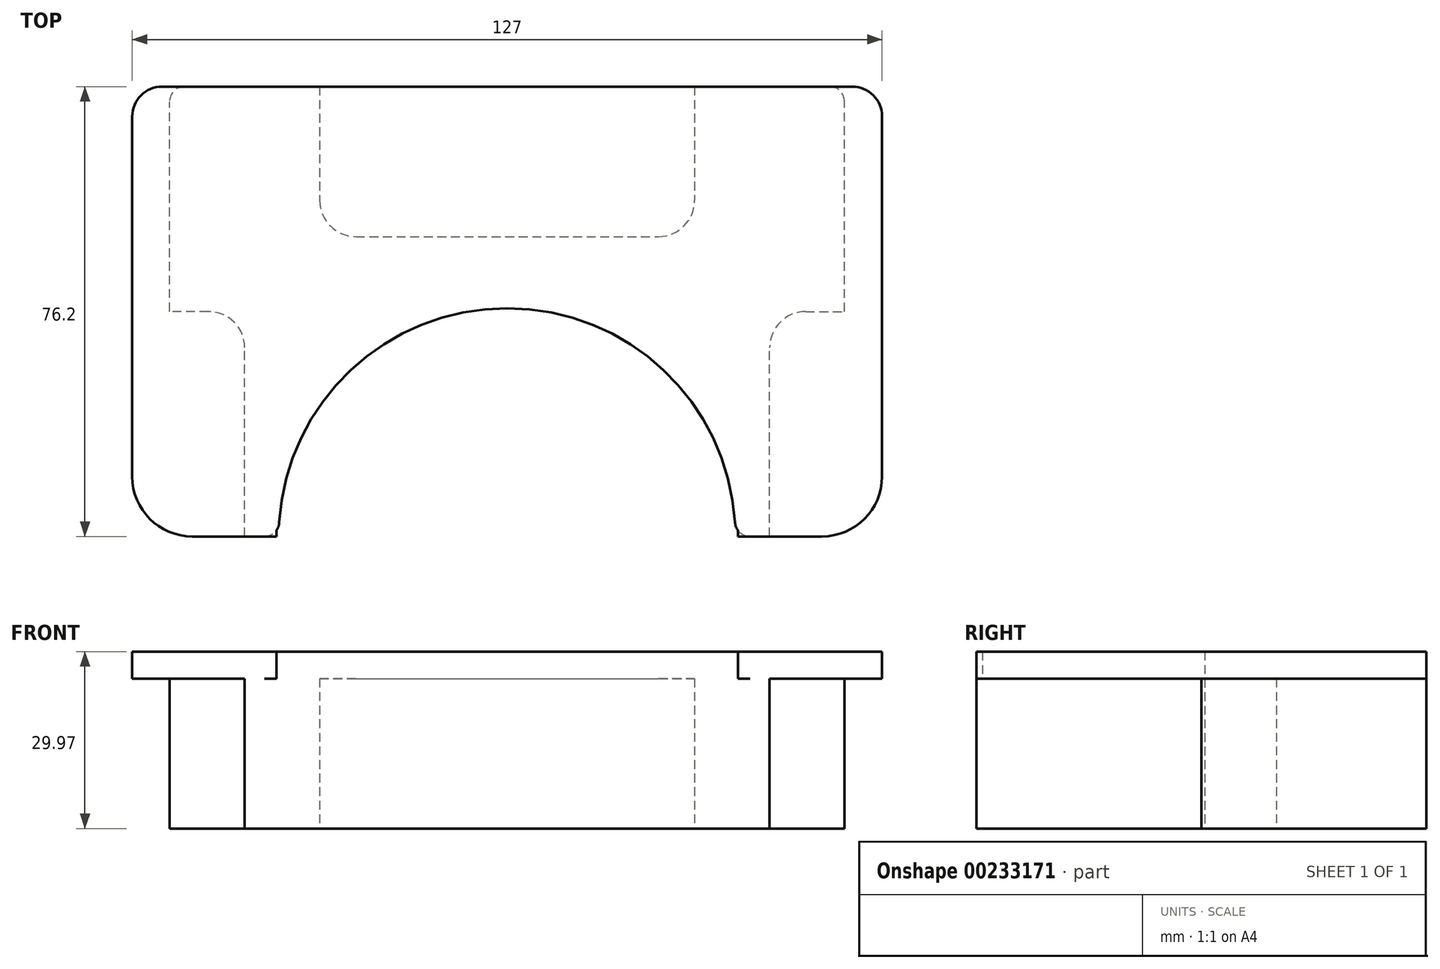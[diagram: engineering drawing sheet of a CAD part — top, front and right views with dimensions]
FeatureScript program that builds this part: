
annotation { "Feature Type Name" : "Feature", "Feature Type Description" : "" }
export const myFeature = defineFeature(function(context is Context, id is Id, definition is map)
    precondition{}
    {
        {
            var Q0;
            Q0=qCreatedBy(makeId("Top.planeOp"),FACE);
            var sketch = newSketch(context, id + "F0", { "sketchPlane" : qUnion([Q0])});
            skLineSegment(sketch, "E0.bottom", {"start": v(-63.5, 38.1) * mm, "end": v(63.5, 38.1) * mm});
            skLineSegment(sketch, "E0.top", {"start": v(-63.5, -38.1) * mm, "end": v(63.5, -38.1) * mm});
            skLineSegment(sketch, "E0.left", {"start": v(-63.5, 38.1) * mm, "end": v(-63.5, -38.1) * mm});
            skLineSegment(sketch, "E0.right", {"start": v(63.5, 38.1) * mm, "end": v(63.5, -38.1) * mm});
            skPoint(sketch, "E0.middle", {"position": v(0, 0) * mm});
            skSolve(sketch);
        }
        {
            var Q0;
            Q0 = qSketchRegion(id + "F0", true);
            extrude(context, id + "F1", {"entities" : qUnion([Q0]), "depth" : 4.57 * mm});
        }
        {
            var Q0;
            Q0=makeQuery(id+"F1.opExtrude","CAP_FACE",FACE,{"disambiguationData":[OSD([sQuery(id+"F0.wireOp",EDGE,"E0.bottom"),sQuery(id+"F0.wireOp",EDGE,"E0.top"),sQuery(id+"F0.wireOp",EDGE,"E0.left"),sQuery(id+"F0.wireOp",EDGE,"E0.right")])],"isStart":true});
            var sketch = newSketch(context, id + "F2", { "sketchPlane" : qUnion([Q0])});
            skLineSegment(sketch, "E1.bottom", {"start": v(57.15, 38.1) * mm, "end": v(-57.15, 38.1) * mm});
            skLineSegment(sketch, "E1.top", {"start": v(57.15, -38.1) * mm, "end": v(-57.15, -38.1) * mm});
            skLineSegment(sketch, "E1.left", {"start": v(57.15, 38.1) * mm, "end": v(57.15, -38.1) * mm});
            skLineSegment(sketch, "E1.right", {"start": v(-57.15, 38.1) * mm, "end": v(-57.15, -38.1) * mm});
            skSolve(sketch);
        }
        {
            var Q0;
            Q0 = qSketchRegion(id + "F2", true);
            extrude(context, id + "F3", {"entities" : qUnion([Q0]), "operationType" : NewBodyOperationType.ADD, "depth" : 25.4 * mm});
        }
        {
            var Q0;
            Q0=makeQuery(id+"F3.opExtrude","CAP_FACE",FACE,{"disambiguationData":[OSD([sQuery(id+"F2.wireOp",EDGE,"E1.bottom"),sQuery(id+"F2.wireOp",EDGE,"E1.top"),sQuery(id+"F2.wireOp",EDGE,"E1.left"),sQuery(id+"F2.wireOp",EDGE,"E1.right")])],"isStart":false});
            var sketch = newSketch(context, id + "F4", { "sketchPlane" : qUnion([Q0])});
            skLineSegment(sketch, "E2.bottom", {"start": v(-31.75, -38.1) * mm, "end": v(31.75, -38.1) * mm});
            skLineSegment(sketch, "E2.top", {"start": v(-31.75, -12.7) * mm, "end": v(31.75, -12.7) * mm});
            skLineSegment(sketch, "E2.left", {"start": v(-31.75, -38.1) * mm, "end": v(-31.75, -12.7) * mm});
            skLineSegment(sketch, "E2.right", {"start": v(31.75, -38.1) * mm, "end": v(31.75, -12.7) * mm});
            skLineSegment(sketch, "E3.bottom", {"start": v(-44.45, 38.1) * mm, "end": v(-57.15, 38.1) * mm});
            skLineSegment(sketch, "E3.top", {"start": v(-44.45, 0) * mm, "end": v(-57.15, 0) * mm});
            skLineSegment(sketch, "E3.left", {"start": v(-44.45, 38.1) * mm, "end": v(-44.45, 0) * mm});
            skLineSegment(sketch, "E3.right", {"start": v(-57.15, 38.1) * mm, "end": v(-57.15, 0) * mm});
            skLineSegment(sketch, "E4.bottom", {"start": v(44.45, 38.1) * mm, "end": v(57.15, 38.1) * mm});
            skLineSegment(sketch, "E4.top", {"start": v(44.45, 0) * mm, "end": v(57.15, 0) * mm});
            skLineSegment(sketch, "E4.left", {"start": v(44.45, 38.1) * mm, "end": v(44.45, 0) * mm});
            skLineSegment(sketch, "E4.right", {"start": v(57.15, 38.1) * mm, "end": v(57.15, 0) * mm});
            skCircle(sketch, "E5", {"center": v(0, 38.1) * mm, "radius": 38.67 * mm});
            skSolve(sketch);
        }
        {
            var Q0;
            Q0 = qSketchRegion(id + "F4", true);
            extrude(context, id + "F5", {"entities" : qUnion([Q0]), "operationType" : NewBodyOperationType.REMOVE, "oppositeDirection" : true, "depth" : 25.4 * mm});
        }
        {
            var Q0;
            Q0=makeQuery(id+"F1.opExtrude","SWEPT_EDGE",EDGE,{"disambiguationData":[OSD([sQuery(id+"F0.wireOp",EDGE,"E0.top"),sQuery(id+"F0.wireOp",EDGE,"E0.left")])]});
            fillet(context, id + "F6", {"entities" : qUnion([Q0]), "radius" : 10.16 * mm, "tangentPropagation" : true, "allowEdgeOverflow" : false});
        }
        {
            var Q0;
            Q0=makeQuery(id+"F5.boolean.opBoolean","COPY",EDGE,{"derivedFrom":makeQuery(id+"F5.opExtrude","SWEPT_EDGE",EDGE,{"disambiguationData":[OSD([sQuery(id+"F2.wireOp",EDGE,"E1.bottom"),sQuery(id+"F4.wireOp",EDGE,"E3.bottom"),sQuery(id+"F4.wireOp",EDGE,"E3.left")])]})});
            var Q1;
            Q1=makeQuery(id+"F5.boolean.opBoolean","INTERSECT",EDGE,{"disambiguationData":[OD(0.0)],"derivedFrom":[makeQuery(id+"F3.boolean.opBoolean","MERGE",FACE,{"derivedFrom":[makeQuery(id+"F1.opExtrude","SWEPT_FACE",FACE,{"disambiguationData":[OSD([sQuery(id+"F0.wireOp",EDGE,"E0.top")])]}),makeQuery(id+"F3.opExtrude","SWEPT_FACE",FACE,{"disambiguationData":[OSD([sQuery(id+"F2.wireOp",EDGE,"E1.bottom")])]})]}),makeQuery(id+"F5.opExtrude","SWEPT_FACE",FACE,{"disambiguationData":[OSD([sQuery(id+"F4.wireOp",EDGE,"E5")])]})]});
            var Q2;
            Q2=makeQuery(id+"F5.boolean.opBoolean","COPY",EDGE,{"derivedFrom":makeQuery(id+"F5.opExtrude","SWEPT_EDGE",EDGE,{"disambiguationData":[OSD([sQuery(id+"F2.wireOp",EDGE,"E1.bottom"),sQuery(id+"F4.wireOp",EDGE,"E4.bottom"),sQuery(id+"F4.wireOp",EDGE,"E4.left")])]})});
            var Q3;
            Q3=makeQuery(id+"F5.boolean.opBoolean","INTERSECT",EDGE,{"disambiguationData":[OD(1.0)],"derivedFrom":[makeQuery(id+"F3.boolean.opBoolean","MERGE",FACE,{"derivedFrom":[makeQuery(id+"F1.opExtrude","SWEPT_FACE",FACE,{"disambiguationData":[OSD([sQuery(id+"F0.wireOp",EDGE,"E0.top")])]}),makeQuery(id+"F3.opExtrude","SWEPT_FACE",FACE,{"disambiguationData":[OSD([sQuery(id+"F2.wireOp",EDGE,"E1.bottom")])]})]}),makeQuery(id+"F5.opExtrude","SWEPT_FACE",FACE,{"disambiguationData":[OSD([sQuery(id+"F4.wireOp",EDGE,"E5")])]})]});
            var Q4;
            Q4=makeQuery(id+"F5.boolean.opBoolean","COPY",EDGE,{"derivedFrom":makeQuery(id+"F5.opExtrude","SWEPT_EDGE",EDGE,{"disambiguationData":[OSD([sQuery(id+"F2.wireOp",EDGE,"E1.left"),sQuery(id+"F4.wireOp",EDGE,"E4.top"),sQuery(id+"F4.wireOp",EDGE,"E4.right")])]})});
            var Q5;
            Q5=makeQuery(id+"F5.boolean.opBoolean","COPY",EDGE,{"derivedFrom":makeQuery(id+"F5.opExtrude","SWEPT_EDGE",EDGE,{"disambiguationData":[OSD([sQuery(id+"F2.wireOp",EDGE,"E1.right"),sQuery(id+"F4.wireOp",EDGE,"E3.top"),sQuery(id+"F4.wireOp",EDGE,"E3.right")])]})});
            var Q6;
            Q6=makeQuery(id+"F5.boolean.opBoolean","COPY",EDGE,{"derivedFrom":makeQuery(id+"F5.opExtrude","SWEPT_EDGE",EDGE,{"disambiguationData":[OSD([sQuery(id+"F2.wireOp",EDGE,"E1.top"),sQuery(id+"F4.wireOp",EDGE,"E2.bottom"),sQuery(id+"F4.wireOp",EDGE,"E2.left")])]})});
            var Q7;
            Q7=makeQuery(id+"F3.opExtrude","SWEPT_EDGE",EDGE,{"disambiguationData":[OSD([sQuery(id+"F0.wireOp",EDGE,"E0.bottom"),sQuery(id+"F2.wireOp",EDGE,"E1.top"),sQuery(id+"F2.wireOp",EDGE,"E1.right")])]});
            var Q8;
            Q8=makeQuery(id+"F3.opExtrude","SWEPT_EDGE",EDGE,{"disambiguationData":[OSD([sQuery(id+"F0.wireOp",EDGE,"E0.bottom"),sQuery(id+"F2.wireOp",EDGE,"E1.top"),sQuery(id+"F2.wireOp",EDGE,"E1.left")])]});
            var Q9;
            Q9=makeQuery(id+"F5.boolean.opBoolean","COPY",EDGE,{"derivedFrom":makeQuery(id+"F5.opExtrude","SWEPT_EDGE",EDGE,{"disambiguationData":[OSD([sQuery(id+"F2.wireOp",EDGE,"E1.top"),sQuery(id+"F4.wireOp",EDGE,"E2.bottom"),sQuery(id+"F4.wireOp",EDGE,"E2.right")])]})});
            fillet(context, id + "F7", {"entities" : qUnion([Q0, Q1, Q2, Q3, Q4, Q5, Q6, Q7, Q8, Q9]), "radius" : 2.54 * mm, "tangentPropagation" : true, "allowEdgeOverflow" : false});
        }
        {
            var Q0;
            Q0=makeQuery(id+"F5.boolean.opBoolean","COPY",EDGE,{"derivedFrom":makeQuery(id+"F5.opExtrude","SWEPT_EDGE",EDGE,{"disambiguationData":[OSD([sQuery(id+"F4.wireOp",EDGE,"E3.top"),sQuery(id+"F4.wireOp",EDGE,"E3.left")])]})});
            var Q1;
            Q1=makeQuery(id+"F5.boolean.opBoolean","COPY",EDGE,{"derivedFrom":makeQuery(id+"F5.opExtrude","SWEPT_EDGE",EDGE,{"disambiguationData":[OSD([sQuery(id+"F4.wireOp",EDGE,"E4.top"),sQuery(id+"F4.wireOp",EDGE,"E4.left")])]})});
            var Q2;
            Q2=makeQuery(id+"F5.boolean.opBoolean","COPY",EDGE,{"derivedFrom":makeQuery(id+"F5.opExtrude","SWEPT_EDGE",EDGE,{"disambiguationData":[OSD([sQuery(id+"F4.wireOp",EDGE,"E2.top"),sQuery(id+"F4.wireOp",EDGE,"E2.left")])]})});
            var Q3;
            Q3=makeQuery(id+"F5.boolean.opBoolean","COPY",EDGE,{"derivedFrom":makeQuery(id+"F5.opExtrude","SWEPT_EDGE",EDGE,{"disambiguationData":[OSD([sQuery(id+"F4.wireOp",EDGE,"E2.top"),sQuery(id+"F4.wireOp",EDGE,"E2.right")])]})});
            fillet(context, id + "F8", {"entities" : qUnion([Q0, Q1, Q2, Q3]), "radius" : 6.13 * mm, "tangentPropagation" : true, "allowEdgeOverflow" : false});
        }
        {
            var Q0;
            Q0=makeQuery(id+"F1.opExtrude","SWEPT_EDGE",EDGE,{"disambiguationData":[OSD([sQuery(id+"F0.wireOp",EDGE,"E0.bottom"),sQuery(id+"F0.wireOp",EDGE,"E0.left")])]});
            var Q1;
            Q1=makeQuery(id+"F1.opExtrude","SWEPT_EDGE",EDGE,{"disambiguationData":[OSD([sQuery(id+"F0.wireOp",EDGE,"E0.bottom"),sQuery(id+"F0.wireOp",EDGE,"E0.right")])]});
            fillet(context, id + "F9", {"entities" : qUnion([Q0, Q1]), "radius" : 5.08 * mm, "tangentPropagation" : true, "allowEdgeOverflow" : false});
        }
        {
            var Q0;
            Q0=makeQuery(id+"F1.opExtrude","SWEPT_EDGE",EDGE,{"disambiguationData":[OSD([sQuery(id+"F0.wireOp",EDGE,"E0.top"),sQuery(id+"F0.wireOp",EDGE,"E0.right")])]});
            fillet(context, id + "F10", {"entities" : qUnion([Q0]), "radius" : 10.16 * mm, "tangentPropagation" : true, "allowEdgeOverflow" : false});
        }
        {
            var Q0;
            Q0=makeQuery(id+"F5.boolean.opBoolean","COPY",FACE,{"derivedFrom":makeQuery(id+"F5.opExtrude","CAP_FACE",FACE,{"disambiguationData":[OSD([sQuery(id+"F4.wireOp",EDGE,"E5")])],"isStart":false})});
            var sketch = newSketch(context, id + "F11", { "sketchPlane" : qUnion([Q0])});
            skCircle(sketch, "E6", {"center": v(0, 38.1) * mm, "radius": 39.1 * mm});
            skSolve(sketch);
        }
        {
            var Q0;
            {var subQ0=sQuery(id+"F4.wireOp",EDGE,"E5");var subQ1=makeQuery(id+"F5.boolean.opBoolean","COPY",EDGE,{"derivedFrom":makeQuery(id+"F5.opExtrude","CAP_EDGE",EDGE,{"disambiguationData":[OSD([subQ0])],"isStart":false})});Q0=makeQuery(id+"F11.imprint","IMPRINT",FACE,{"disambiguationData":[TD([[makeQuery(id+"F11.imprint","IMPRINT",EDGE,{"derivedFrom":subQ1}),1.0]])]});}
            extrude(context, id + "F12", {"entities" : qUnion([Q0]), "operationType" : NewBodyOperationType.REMOVE, "oppositeDirection" : true, "depth" : 5.08 * mm});
        }
    });
